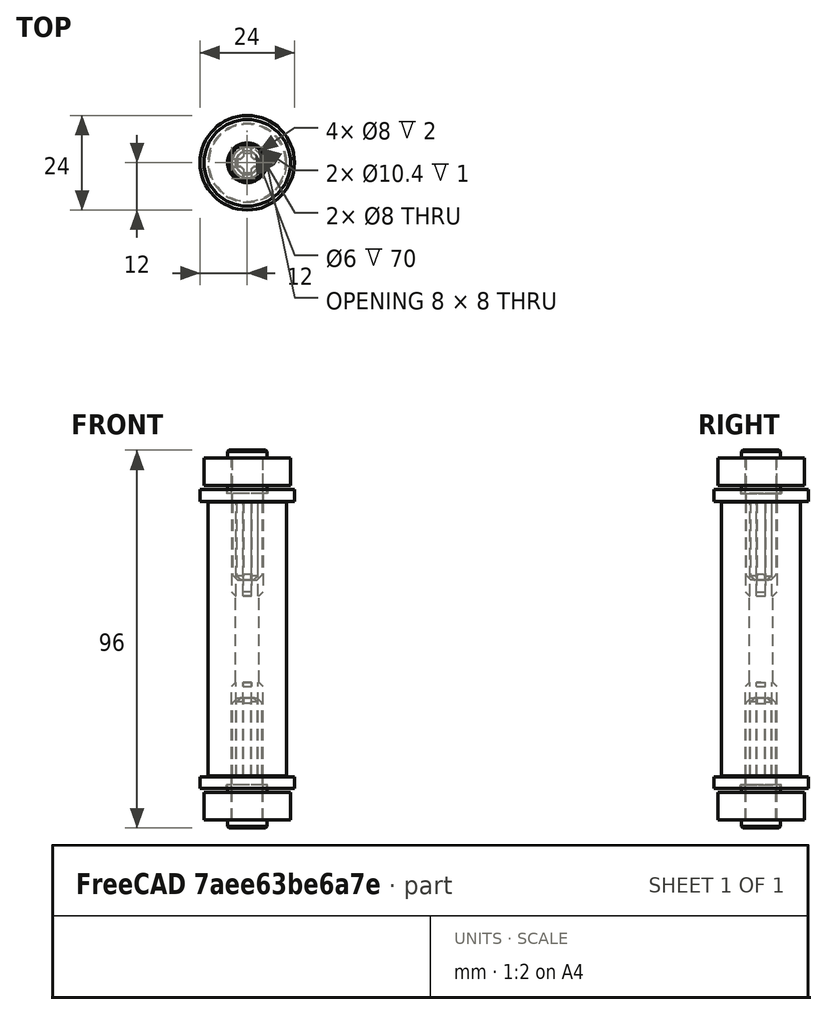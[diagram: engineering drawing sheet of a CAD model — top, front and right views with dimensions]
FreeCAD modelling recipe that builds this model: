
FCSTD DOCUMENT  (FreeCAD 0.18R14555 (Git shallow))
Label: roller
License: All rights reserved
LicenseURL: http://en.wikipedia.org/wiki/All_rights_reserved
objects: Part::Cylinder×13, Part::Cut×7, Part::Chamfer×5, Part::Feature×5, Part::Box×4, Part::MultiFuse×3, Part::MultiCommon×1
note: 38 computed .brp shape members not serialized (recipe doc carries the construction recipe); baked Part::Feature solids carry a one-line shape summary decoded from their .brp

FEATURE [Part::Cylinder] Cylinder002
  Angle = 360
  AttacherType = Attacher::AttachEngine3D
  Height = 70
  Placement = pos=(0,0,9) rot=(0,0,1;0rad)
  Radius = 10
FEATURE [Part::Cylinder] Cylinder
  Angle = 360
  AttacherType = Attacher::AttachEngine3D
  Height = 3
  Radius = 12
FEATURE [Part::Cylinder] Cylinder003
  Angle = 360
  AttacherType = Attacher::AttachEngine3D
  Height = 3
  Placement = pos=(0,0,-2) rot=(0,0,1;0rad)
  Radius = 5.2
FEATURE [Part::Cut] Cut
  Base = -> Cylinder
  Tool = -> Cylinder003
FEATURE [Part::Cylinder] Cylinder004
  Angle = 360
  AttacherType = Attacher::AttachEngine3D
  Height = 10
  Radius = 4
FEATURE [Part::Cut] Cut001
  Base = -> Cut
  Placement = pos=(0,0,6) rot=(0,0,1;0rad)
  Tool = -> Cylinder004
FEATURE [Part::Cylinder] Cylinder005
  Angle = 360
  AttacherType = Attacher::AttachEngine3D
  Height = 2
  Placement = pos=(0,0,-6) rot=(0,0,1;0rad)
  Radius = 5
FEATURE [Part::Cylinder] Cylinder006
  Angle = 360
  AttacherType = Attacher::AttachEngine3D
  Height = 2
  Placement = pos=(0,0,-6) rot=(0,0,1;0rad)
  Radius = 4
FEATURE [Part::Cut] Cut002
  Base = -> Cylinder005
  Placement = pos=(0,0,11) rot=(0,0,1;0rad)
  Tool = -> Cylinder006
FEATURE [Part::Cylinder] Cylinder007
  Angle = 360
  AttacherType = Attacher::AttachEngine3D
  Height = 7
  Radius = 11
FEATURE [Part::Cylinder] Cylinder008
  Angle = 360
  AttacherType = Attacher::AttachEngine3D
  Height = 7
  Radius = 4
FEATURE [Part::Cut] Cut003
  Base = -> Cylinder007
  Placement = pos=(0,0,-2) rot=(0,0,1;0rad)
  Tool = -> Cylinder008
FEATURE [Part::Cylinder] Cylinder009
  Angle = 360
  AttacherType = Attacher::AttachEngine3D
  Height = 2
  Placement = pos=(0,0,-4) rot=(0,0,1;0rad)
  Radius = 5
FEATURE [Part::Cylinder] Cylinder010
  Angle = 360
  AttacherType = Attacher::AttachEngine3D
  Height = 11
  Placement = pos=(0,0,-2) rot=(0,0,1;0rad)
  Radius = 3.85
FEATURE [Part::Cylinder] Cylinder011
  Angle = 360
  AttacherType = Attacher::AttachEngine3D
  Height = 70
  Placement = pos=(0,0,9) rot=(0,0,1;0rad)
  Radius = 3
FEATURE [Part::Box] Box  label="Cube"
  AttacherType = Attacher::AttachEngine3D
  Height = 24
  Length = 2.2
  Placement = pos=(-1.1,-4,9) rot=(0,0,1;0rad)
  Width = 8
FEATURE [Part::Box] Box001  label="Cube001"
  AttacherType = Attacher::AttachEngine3D
  Height = 24
  Length = 8
  Placement = pos=(-4,-1.1,9) rot=(0,0,1;0rad)
  Width = 2.2
FEATURE [Part::MultiFuse] Fusion
  Shapes = -> [Box001,Box]
FEATURE [Part::Chamfer] Chamfer
  Base = -> Fusion
  Edges = 4 edges r=1: [Edge2,Edge26,Edge30,Edge33]
FEATURE [Part::Feature] Chamfer001
  Placement = pos=(-1.1e-14,0,88) rot=(0,1,0;3.14159rad)
  shape: bbox 8 x 8 x 24 mm, 26 faces (baked)
FEATURE [Part::Cut] Cut004
  Base = -> Cylinder002
  Tool = -> Cylinder011
FEATURE [Part::Cut] Cut005
  Base = -> Cut004
  Tool = -> Chamfer001
FEATURE [Part::Cut] Cut006
  Base = -> Cut005
  Tool = -> Chamfer
FEATURE [Part::Cylinder] Cylinder012
  Angle = 360
  AttacherType = Attacher::AttachEngine3D
  Height = 20
  Placement = pos=(0,0,9) rot=(0,0,1;0rad)
  Radius = 2.86
FEATURE [Part::Box] Box002  label="Cube002"
  AttacherType = Attacher::AttachEngine3D
  Height = 20
  Length = 8
  Placement = pos=(-4,-1,9) rot=(0,0,1;0rad)
  Width = 2
FEATURE [Part::Box] Box003  label="Cube003"
  AttacherType = Attacher::AttachEngine3D
  Height = 20
  Length = 2
  Placement = pos=(-1,-4,9) rot=(0,0,1;0rad)
  Width = 8
FEATURE [Part::MultiFuse] Fusion002
  Shapes = -> [Box002,Box003]
FEATURE [Part::Chamfer] Chamfer002
  Base = -> Fusion002
  Edges = 4 edges r=1.5: [Edge2,Edge26,Edge30,Edge33]
FEATURE [Part::Cylinder] Cylinder013
  Angle = 360
  AttacherType = Attacher::AttachEngine3D
  Height = 20
  Placement = pos=(0,0,9) rot=(0,0,1;0rad)
  Radius = 3.9
FEATURE [Part::MultiCommon] Common
  Shapes = -> [Chamfer002,Cylinder013]
FEATURE [Part::Chamfer] Chamfer003
  Base = -> Cylinder012
  Edges = 1 edges r=1: [Edge1]
FEATURE [Part::MultiFuse] Fusion003
  Shapes = -> [Common,Chamfer003,Cylinder010,Cylinder009]
FEATURE [Part::Chamfer] Chamfer004
  Base = -> Cut006
  Edges = 2 edges r=0.2: [Edge1,Edge3]
FEATURE [Part::Chamfer] Chamfer005
  Base = -> Fusion003
  Edges = 1 edges r=0.4: [Edge39]
FEATURE [Part::Feature] Cut001001  label="Cut007"
  Placement = pos=(0,9.3e-15,82) rot=(1,0,0;3.14159rad)
  shape: bbox 24 x 24 x 3 mm, 6 faces (baked)
FEATURE [Part::Feature] Cut002001  label="Cut008"
  Placement = pos=(0,0,87) rot=(0,0,1;0rad)
  shape: bbox 10 x 10 x 2 mm, 4 faces (baked)
FEATURE [Part::Feature] Cut003001  label="Cut009"
  Placement = pos=(0,0,83) rot=(0,0,1;0rad)
  shape: bbox 22 x 22 x 7 mm, 4 faces (baked)
FEATURE [Part::Feature] Chamfer005001  label="Chamfer006"
  Placement = pos=(0,1.08e-14,88) rot=(1,0,0;3.14159rad)
  shape: bbox 10 x 10 x 33 mm, 51 faces (baked)
